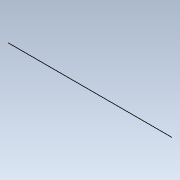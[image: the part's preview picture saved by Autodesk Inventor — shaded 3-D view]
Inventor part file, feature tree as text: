
AUTODESK INVENTOR PART (.ipt)
format: ipt  version: 2021 (Build 250183000, 183)  size: 62,464 bytes
history: native  units: mm
features: sketch x1
ambient origin geometry x8: Origin, YZ Plane, XZ Plane, XY Plane, X Axis, Y Axis, Z Axis, Center Point
feature tree (1):
  sketch  "Sketch1"
